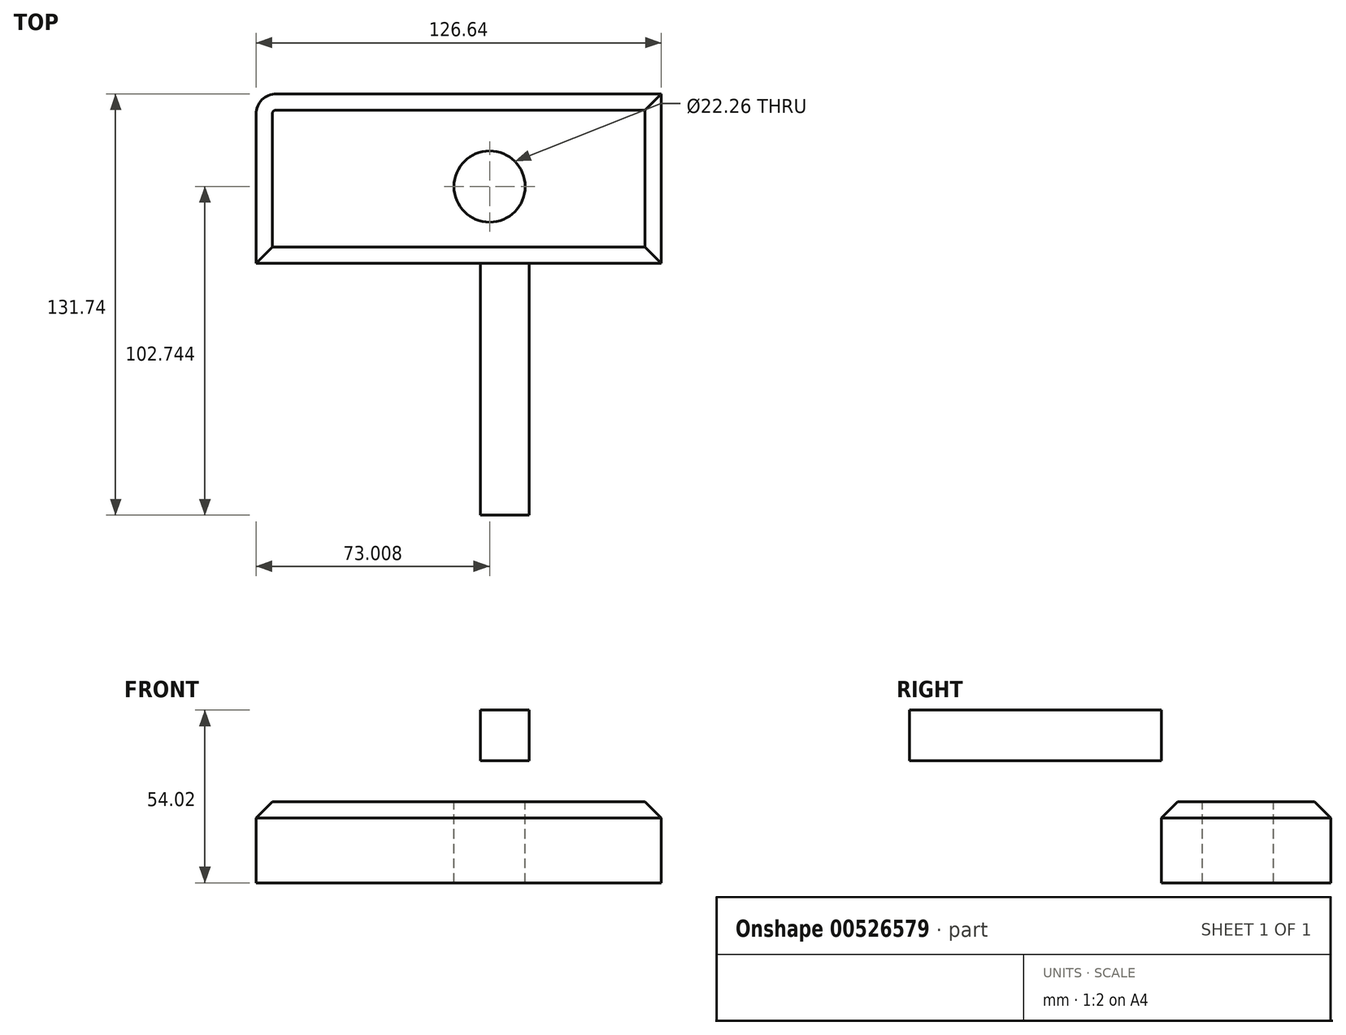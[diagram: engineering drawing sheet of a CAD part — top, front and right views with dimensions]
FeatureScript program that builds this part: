
annotation { "Feature Type Name" : "Feature", "Feature Type Description" : "" }
export const myFeature = defineFeature(function(context is Context, id is Id, definition is map)
    precondition{}
    {
        {
            var Q0;
            Q0=qCreatedBy(makeId("Top.planeOp"),FACE);
            var sketch = newSketch(context, id + "F0", { "sketchPlane" : qUnion([Q0])});
            skLineSegment(sketch, "E0", {"start": v(0, 0) * mm, "end": v(-126.64, 0) * mm});
            skLineSegment(sketch, "E1", {"start": v(-126.64, 0) * mm, "end": v(-126.64, 46.65) * mm});
            skLineSegment(sketch, "E2", {"start": v(-120.3, 53) * mm, "end": v(0, 53) * mm});
            skLineSegment(sketch, "E3", {"start": v(0, 53) * mm, "end": v(0, 0) * mm});
            skPoint(sketch, "E4.visualSharp", {"position": v(-126.64, 53) * mm});
            skArc(sketch, "E4.filletArc", {"start": v(-120.3, 53) * mm, "mid": v(-124.78, 51.14) * mm, "end": v(-126.64, 46.65) * mm});
            skSolve(sketch);
        }
        {
            var Q0;
            Q0 = qSketchRegion(id + "F0", true);
            extrude(context, id + "F1", {"entities" : qUnion([Q0]), "depth" : 25.4 * mm, "offsetDistance" : 25.4 * mm});
        }
        {
            var Q0;
            Q0=makeQuery(id+"F1.opExtrude","CAP_EDGE",EDGE,{"disambiguationData":[OSD([sQuery(id+"F0.wireOp",EDGE,"E1")])],"isStart":false});
            var Q1;
            Q1=makeQuery(id+"F1.opExtrude","CAP_EDGE",EDGE,{"disambiguationData":[OSD([sQuery(id+"F0.wireOp",EDGE,"E0")])],"isStart":false});
            var Q2;
            Q2=makeQuery(id+"F1.opExtrude","CAP_EDGE",EDGE,{"disambiguationData":[OSD([sQuery(id+"F0.wireOp",EDGE,"E3")])],"isStart":false});
            chamfer(context, id + "F2", {"entities" : qUnion([Q0, Q1, Q2]), "width" : 5.08 * mm, "tangentPropagation" : true});
        }
        {
            var Q0;
            Q0=makeQuery(id+"F1.opExtrude","CAP_FACE",FACE,{"disambiguationData":[OSD([sQuery(id+"F0.wireOp",EDGE,"E0"),sQuery(id+"F0.wireOp",EDGE,"E1"),sQuery(id+"F0.wireOp",EDGE,"E2"),sQuery(id+"F0.wireOp",EDGE,"E3"),sQuery(id+"F0.wireOp",EDGE,"E4.filletArc")])],"isStart":false});
            var sketch = newSketch(context, id + "F3", { "sketchPlane" : qUnion([Q0])});
            skCircle(sketch, "E5", {"center": v(-53.63, 24) * mm, "radius": 11.13 * mm});
            skSolve(sketch);
        }
        {
            var Q0;
            Q0=makeQuery(id+"F3.imprint","IMPRINT",FACE,{"disambiguationData":[TD([[makeQuery(id+"F3.imprint","IMPRINT",EDGE,{"derivedFrom":sQuery(id+"F3.wireOp",EDGE,"E5")}),1.0]])]});
            extrude(context, id + "F4", {"entities" : qUnion([Q0]), "operationType" : NewBodyOperationType.REMOVE, "oppositeDirection" : true, "depth" : 72.14 * mm, "offsetDistance" : 25.4 * mm, "hasSecondDirection" : true, "secondDirectionOppositeDirection" : false, "secondDirectionDepth" : 25.4 * mm});
        }
        {
            var Q0;
            Q0=makeQuery(id+"F1.opExtrude","SWEPT_FACE",FACE,{"disambiguationData":[OSD([sQuery(id+"F0.wireOp",EDGE,"E0")])]});
            var sketch = newSketch(context, id + "F5", { "sketchPlane" : qUnion([Q0])});
            skLineSegment(sketch, "E6.bottom", {"start": v(-56.56, 54.02) * mm, "end": v(-41.27, 54.02) * mm});
            skLineSegment(sketch, "E6.top", {"start": v(-56.56, 38.22) * mm, "end": v(-41.27, 38.22) * mm});
            skLineSegment(sketch, "E6.left", {"start": v(-56.56, 54.02) * mm, "end": v(-56.56, 38.22) * mm});
            skLineSegment(sketch, "E6.right", {"start": v(-41.27, 54.02) * mm, "end": v(-41.27, 38.22) * mm});
            skSolve(sketch);
        }
        {
            var Q0;
            Q0=makeQuery(id+"F5.imprint","IMPRINT",FACE,{"disambiguationData":[TD([[makeQuery(id+"F5.imprint","IMPRINT",EDGE,{"derivedFrom":sQuery(id+"F5.wireOp",EDGE,"E6.bottom")}),-1.0]])]});
            extrude(context, id + "F6", {"entities" : qUnion([Q0]), "depth" : 78.74 * mm, "offsetDistance" : 25.4 * mm});
        }
        {
            var Q0;
            Q0=qCreatedBy(makeId("Front.planeOp"),FACE);
            var sketch = newSketch(context, id + "F7", { "sketchPlane" : qUnion([Q0])});
            skLineSegment(sketch, "E7", {"start": v(-69.42, -66.97) * mm, "end": v(-17.82, -40.04) * mm});
            skSolve(sketch);
        }
    });
